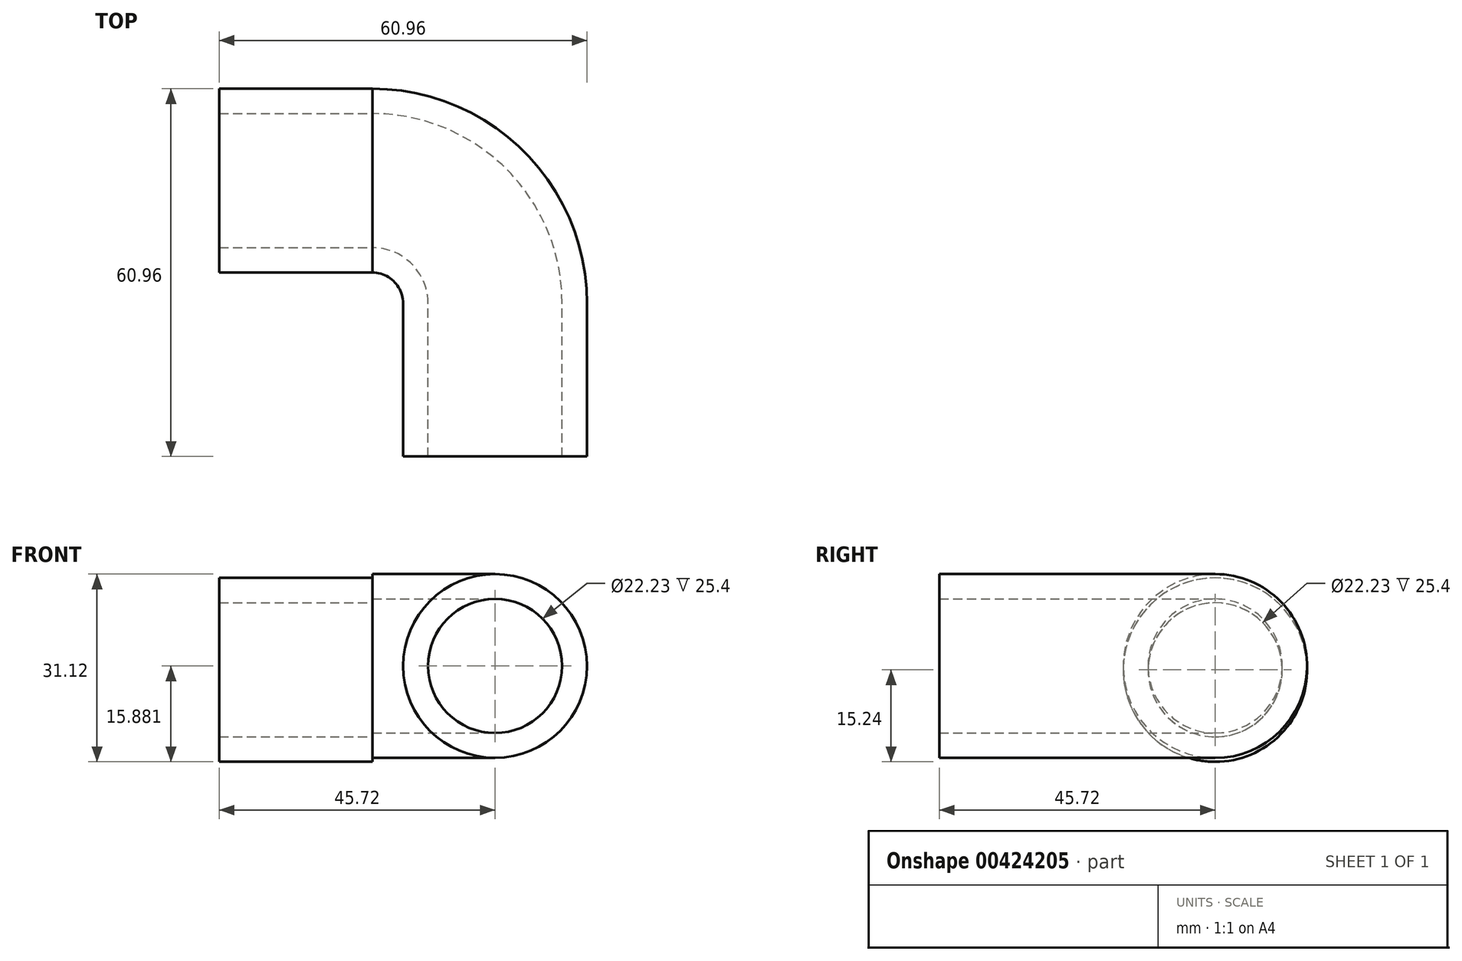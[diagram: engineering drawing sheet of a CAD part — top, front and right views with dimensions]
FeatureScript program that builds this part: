
annotation { "Feature Type Name" : "Feature", "Feature Type Description" : "" }
export const myFeature = defineFeature(function(context is Context, id is Id, definition is map)
    precondition{}
    {
        {
            var Q0;
            Q0=qCreatedBy(makeId("Front.planeOp"),FACE);
            var sketch = newSketch(context, id + "F0", { "sketchPlane" : qUnion([Q0])});
            skPoint(sketch, "E0", {"position": v(20.32, 0.64) * mm});
            skCircle(sketch, "E1", {"center": v(20.32, 0.64) * mm, "radius": 15.24 * mm});
            skCircle(sketch, "E2", {"center": v(20.32, 0.64) * mm, "radius": 11.11 * mm});
            skSolve(sketch);
        }
        {
            var Q0;
            Q0=qCreatedBy(makeId("Right.planeOp"),FACE);
            var sketch = newSketch(context, id + "F1", { "sketchPlane" : qUnion([Q0])});
            skPoint(sketch, "E3", {"position": v(20.32, 0) * mm});
            skCircle(sketch, "E4", {"center": v(20.32, 0) * mm, "radius": 15.24 * mm});
            skCircle(sketch, "E5", {"center": v(20.32, 0) * mm, "radius": 11.11 * mm});
            skSolve(sketch);
        }
        {
            var Q0;
            Q0=qSketchRegion(id+"F0",true);
            extrude(context, id + "F2", {"entities" : qUnion([Q0]), "depth" : 25.4 * mm});
        }
        {
            var Q0;
            Q0=qSketchRegion(id+"F1",true);
            extrude(context, id + "F3", {"entities" : qUnion([Q0]), "operationType" : NewBodyOperationType.ADD, "oppositeDirection" : true, "depth" : 25.4 * mm});
        }
        {
            var Q0;
            Q0=qCreatedBy(makeId("Top.planeOp"),FACE);
            var sketch = newSketch(context, id + "F4", { "sketchPlane" : qUnion([Q0])});
            skPoint(sketch, "E6", {"position": v(0, 35.47) * mm});
            skPoint(sketch, "E7", {"position": v(35.47, 0) * mm});
            skArc(sketch, "E8", {"start": v(35.47, 0) * mm, "mid": v(25.08, 25.08) * mm, "end": v(0, 35.47) * mm});
            skSolve(sketch);
        }
        {
            var Q0;
            Q0=makeQuery(id+"F2.opExtrude","CAP_FACE",FACE,{"disambiguationData":[OSD([sQuery(id+"F0.wireOp",EDGE,"E1"),sQuery(id+"F0.wireOp",EDGE,"E2")])],"isStart":true});
            var Q1;
            Q1=sQuery(id+"F4.wireOp",EDGE,"E8");
            sweep(context, id + "F5", {"operationType" : NewBodyOperationType.ADD, "profiles" : qUnion([Q0]), "path" : qUnion([Q1])});
        }
    });
